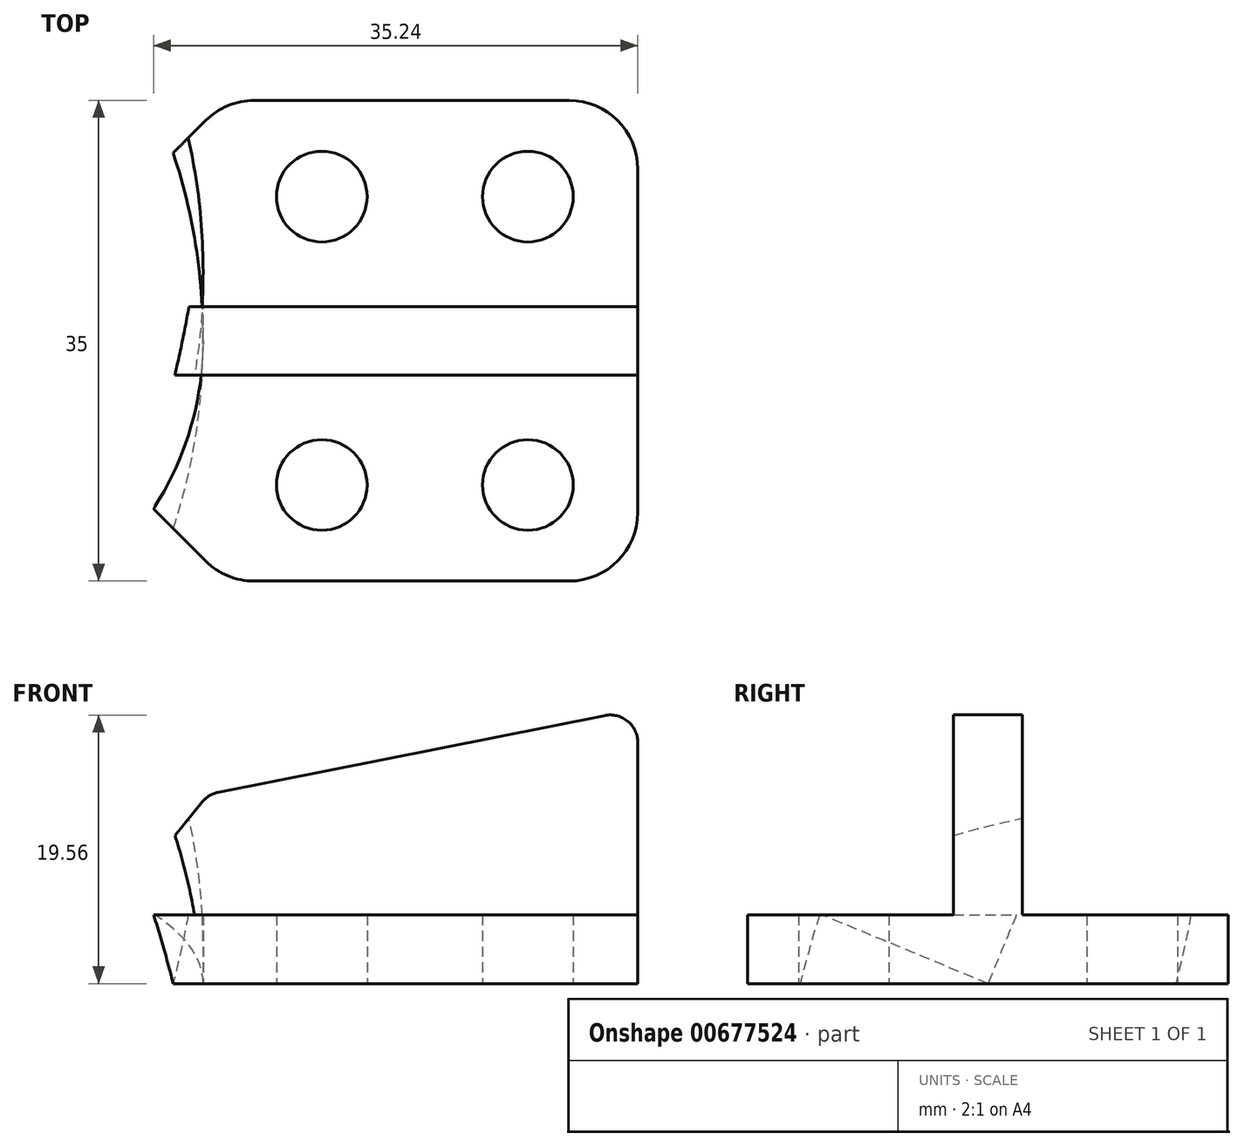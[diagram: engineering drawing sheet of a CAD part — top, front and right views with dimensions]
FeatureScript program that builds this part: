
annotation { "Feature Type Name" : "Feature", "Feature Type Description" : "" }
export const myFeature = defineFeature(function(context is Context, id is Id, definition is map)
    precondition{}
    {
        {
            var Q0;
            Q0=qCreatedBy(makeId("Top.planeOp"),FACE);
            var sketch = newSketch(context, id + "F0", { "sketchPlane" : qUnion([Q0])});
            skArc(sketch, "E0", {"start": v(14.14, 17.5) * mm, "mid": v(-22.5, 0) * mm, "end": v(14.14, -17.5) * mm, "construction": true});
            skLineSegment(sketch, "E1.bottom", {"start": v(24.14, 17.5) * mm, "end": v(54.14, 17.5) * mm});
            skLineSegment(sketch, "E1.top", {"start": v(24.14, -17.5) * mm, "end": v(54.14, -17.5) * mm});
            skLineSegment(sketch, "E1.right", {"start": v(54.14, 17.5) * mm, "end": v(54.14, -17.5) * mm});
            skPoint(sketch, "E2", {"position": v(54.14, 0) * mm});
            skArc(sketch, "E3", {"start": v(18.88, 12.24) * mm, "mid": v(22.5, 0) * mm, "end": v(18.88, -12.24) * mm});
            skPoint(sketch, "E4", {"position": v(31.14, 10.5) * mm});
            skPoint(sketch, "E5", {"position": v(46.14, 10.5) * mm});
            skPoint(sketch, "E6", {"position": v(46.14, -10.5) * mm});
            skPoint(sketch, "E7", {"position": v(31.14, -10.5) * mm});
            skPoint(sketch, "E8.startSnap0", {"position": v(22.5, 0) * mm});
            skLineSegment(sketch, "E9", {"start": v(18.88, 12.24) * mm, "end": v(24.14, 17.5) * mm});
            skLineSegment(sketch, "E10.MirrorCS", {"start": v(18.88, -12.24) * mm, "end": v(24.14, -17.5) * mm});
            skArc(sketch, "E11.trimOffspring", {"start": v(18.88, -12.24) * mm, "mid": v(22.5, 0) * mm, "end": v(18.88, 12.24) * mm, "construction": true});
            skLineSegment(sketch, "E12", {"start": v(18.88, 12.24) * mm, "end": v(18.88, -12.24) * mm});
            skSolve(sketch);
        }
        {
            var Q0;
            Q0=makeQuery(id+"F0.imprint","IMPRINT",FACE,{"disambiguationData":[TD([[makeQuery(id+"F0.imprint","IMPRINT",EDGE,{"derivedFrom":sQuery(id+"F0.wireOp",EDGE,"E1.bottom")}),-1.0]])]});
            var Q1;
            Q1=makeQuery(id+"F0.imprint","IMPRINT",FACE,{"disambiguationData":[TD([[makeQuery(id+"F0.imprint","IMPRINT",EDGE,{"derivedFrom":sQuery(id+"F0.wireOp",EDGE,"E3")}),-1.0]])]});
            extrude(context, id + "F1", {"entities" : qUnion([Q0, Q1]), "depth" : 5 * mm, "offsetDistance" : 25 * mm});
        }
        {
            var Q0;
            Q0=qCreatedBy(makeId("Front.planeOp"),FACE);
            var sketch = newSketch(context, id + "F2", { "sketchPlane" : qUnion([Q0])});
            skLineSegment(sketch, "E13", {"start": v(18.88, 13) * mm, "end": v(54.14, 20) * mm});
            skLineSegment(sketch, "E14", {"start": v(54.14, 20) * mm, "end": v(54.14, 5) * mm});
            skLineSegment(sketch, "E15", {"start": v(54.14, 5) * mm, "end": v(18.88, 5) * mm});
            skLineSegment(sketch, "E16", {"start": v(18.88, 13) * mm, "end": v(18.88, 5) * mm});
            skSolve(sketch);
        }
        {
            var Q0;
            Q0=makeQuery(id+"F2.imprint","IMPRINT",FACE,{"disambiguationData":[TD([[makeQuery(id+"F2.imprint","IMPRINT",EDGE,{"derivedFrom":sQuery(id+"F2.wireOp",EDGE,"E13")}),-1.0]])]});
            extrude(context, id + "F3", {"entities" : qUnion([Q0]), "operationType" : NewBodyOperationType.ADD, "depth" : 5 * mm, "offsetDistance" : 25 * mm, "symmetric" : true});
        }
        {
            var Q0;
            Q0=makeQuery(id+"F3.opExtrude","SWEPT_EDGE",EDGE,{"disambiguationData":[OSD([sQuery(id+"F2.wireOp",EDGE,"E13"),sQuery(id+"F2.wireOp",EDGE,"E16")])]});
            chamfer(context, id + "F4", {"entities" : qUnion([Q0]), "width" : 5 * mm, "tangentPropagation" : true});
        }
        {
            var Q0;
            {var subQ0=sQuery(id+"F2.wireOp",EDGE,"E13");Q0=makeQuery(id+"F4.opChamfer","BLEND_EDGE",EDGE,{"blendedFrom":[makeQuery(id+"F3.opExtrude","SWEPT_EDGE",EDGE,{"disambiguationData":[OSD([subQ0,sQuery(id+"F2.wireOp",EDGE,"E16")])]}),makeQuery(id+"F3.opExtrude","SWEPT_FACE",FACE,{"disambiguationData":[OSD([subQ0])]})],"blendedInto":[makeQuery(id+"F3.opExtrude","SWEPT_FACE",FACE,{"disambiguationData":[OSD([subQ0])]})]});}
            fillet(context, id + "F5", {"entities" : qUnion([Q0]), "radius" : 2 * mm, "tangentPropagation" : true, "allowEdgeOverflow" : false});
        }
        {
            var Q0;
            Q0=makeQuery(id+"F3.opExtrude","SWEPT_EDGE",EDGE,{"disambiguationData":[OSD([sQuery(id+"F2.wireOp",EDGE,"E13"),sQuery(id+"F2.wireOp",EDGE,"E14")])]});
            fillet(context, id + "F6", {"entities" : qUnion([Q0]), "radius" : 2 * mm, "tangentPropagation" : true, "allowEdgeOverflow" : false});
        }
        {
            var Q0;
            Q0=sQuery(id+"F0.wireOp",VERTEX,"E4");
            var Q1;
            Q1=sQuery(id+"F0.wireOp",VERTEX,"E5");
            var Q2;
            Q2=sQuery(id+"F0.wireOp",VERTEX,"E6");
            var Q3;
            Q3=sQuery(id+"F0.wireOp",VERTEX,"E7");
            var Q4;
            Q4=makeQuery(id+"F1.opExtrude","SWEPT_BODY",BODY,{"disambiguationData":[OSD([sQuery(id+"F0.wireOp",EDGE,"E1.bottom"),sQuery(id+"F0.wireOp",EDGE,"E1.top"),sQuery(id+"F0.wireOp",EDGE,"E1.right"),sQuery(id+"F0.wireOp",EDGE,"E3")])]});
            hole(context, id + "F7", {"style" : HoleStyle.SIMPLE, "endStyle" : HoleEndStyle.BLIND, "oppositeDirection" : true, "standardTappedOrClearance" : lookupTablePath({ "standard" : "ISO", "fit" : "Normal", "size" : "M6", "type" : "Clearance" }), "standardBlindInLast" : lookupTablePath({ "fit" : "Standard", "standard" : "ISO", "size" : "M6", "type" : "Clearance" }), "holeDiameter" : 6.6 * mm, "majorDiameter" : 6 * mm, "holeDepth" : 43 * mm, "isTappedThrough" : true, "tappedDepth" : 40 * mm, "tapClearance" : 3, "startFromSketch" : true, "locations" : qUnion([Q0, Q1, Q2, Q3]), "scope" : qUnion([Q4])});
        }
        {
            var Q0;
            Q0=makeQuery(id+"F1.opExtrude","SWEPT_EDGE",EDGE,{"disambiguationData":[OSD([sQuery(id+"F0.wireOp",EDGE,"E1.top"),sQuery(id+"F0.wireOp",EDGE,"E10.MirrorCS")])]});
            var Q1;
            Q1=makeQuery(id+"F1.opExtrude","SWEPT_EDGE",EDGE,{"disambiguationData":[OSD([sQuery(id+"F0.wireOp",EDGE,"E1.bottom"),sQuery(id+"F0.wireOp",EDGE,"E9")])]});
            var Q2;
            Q2=makeQuery(id+"F1.opExtrude","SWEPT_EDGE",EDGE,{"disambiguationData":[OSD([sQuery(id+"F0.wireOp",EDGE,"E1.top"),sQuery(id+"F0.wireOp",EDGE,"E1.right")])]});
            var Q3;
            Q3=makeQuery(id+"F1.opExtrude","SWEPT_EDGE",EDGE,{"disambiguationData":[OSD([sQuery(id+"F0.wireOp",EDGE,"E1.bottom"),sQuery(id+"F0.wireOp",EDGE,"E1.right")])]});
            fillet(context, id + "F8", {"entities" : qUnion([Q0, Q1, Q2, Q3]), "radius" : 5 * mm, "tangentPropagation" : true, "allowEdgeOverflow" : false});
        }
        {
            var Q0;
            Q0=qCreatedBy(makeId("Front.planeOp"),FACE);
            var Q1;
            Q1=qCreatedBy(makeId("Top.planeOp"),FACE);
            cPlane(context, id + "F9", {"entities" : qUnion([Q0, Q1]), "cplaneType" : CPlaneType.MID_PLANE, "offset" : 25 * mm, "width" : 150 * mm, "height" : 150 * mm});
        }
        {
            var Q0;
            Q0=qCreatedBy(id+"F9.planeOp",FACE);
            var sketch = newSketch(context, id + "F10", { "sketchPlane" : qUnion([Q0])});
            skCircle(sketch, "E17", {"center": v(0, 0) * mm, "radius": 22.5 * mm});
            skSolve(sketch);
        }
        {
            var Q0;
            Q0=makeQuery(id+"F10.imprint","IMPRINT",FACE,{"disambiguationData":[TD([[makeQuery(id+"F10.imprint","IMPRINT",EDGE,{"derivedFrom":sQuery(id+"F10.wireOp",EDGE,"E17")}),1.0]])]});
            extrude(context, id + "F11", {"entities" : qUnion([Q0]), "operationType" : NewBodyOperationType.REMOVE, "depth" : 50 * mm, "offsetDistance" : 25 * mm, "symmetric" : true});
        }
    });
